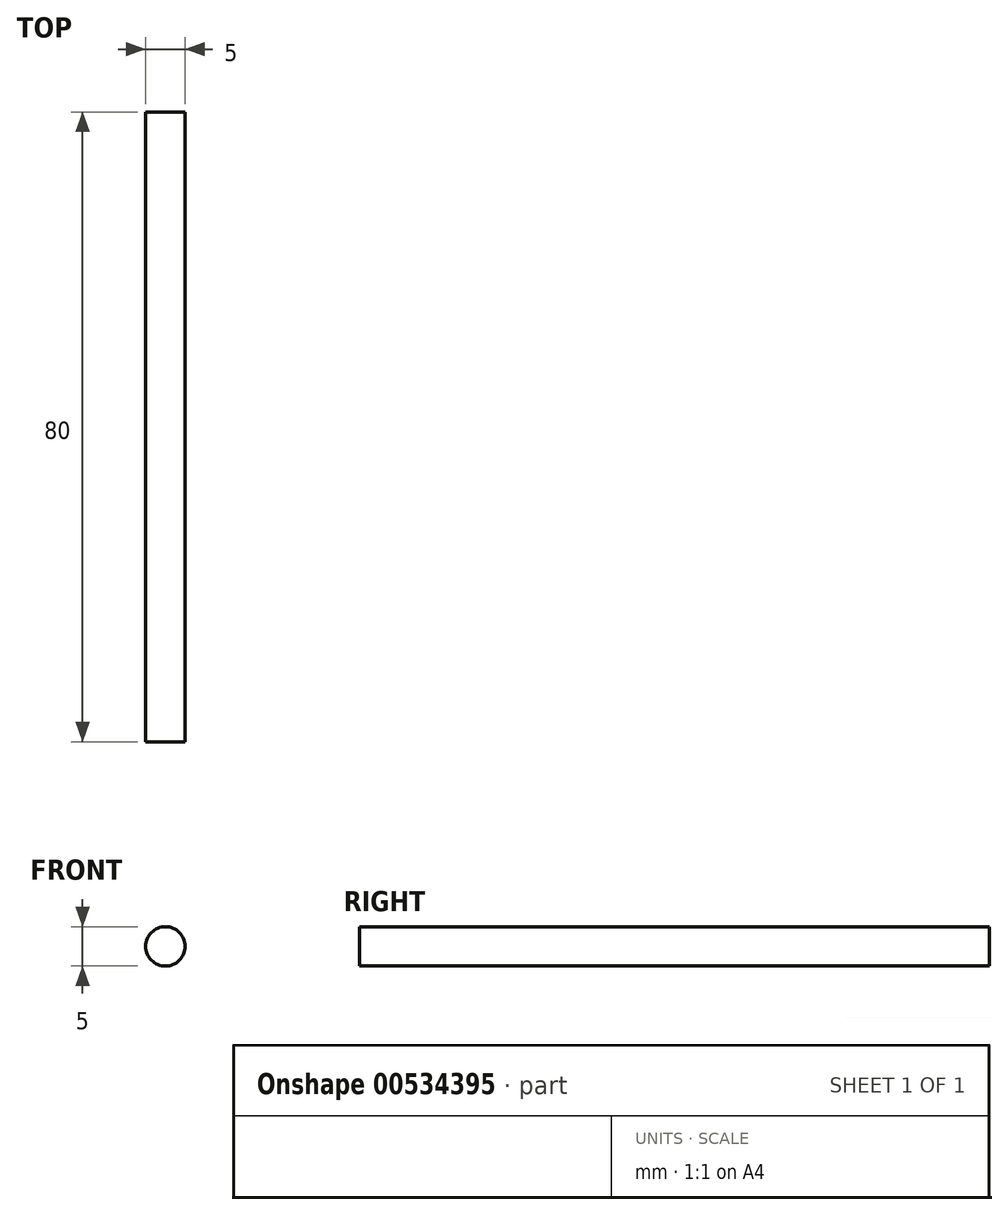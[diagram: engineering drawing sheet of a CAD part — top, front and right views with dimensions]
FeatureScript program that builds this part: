
annotation { "Feature Type Name" : "Feature", "Feature Type Description" : "" }
export const myFeature = defineFeature(function(context is Context, id is Id, definition is map)
    precondition{}
    {
        {
            var Q0;
            Q0=qCreatedBy(makeId("Front.planeOp"),FACE);
            var sketch = newSketch(context, id + "F0", { "sketchPlane" : qUnion([Q0])});
            skCircle(sketch, "E0", {"center": v(0, 0) * mm, "radius": 2.5 * mm});
            skSolve(sketch);
        }
        {
            var Q0;
            Q0 = qSketchRegion(id + "F0", true);
            extrude(context, id + "F1", {"entities" : qUnion([Q0]), "depth" : 80 * mm, "offsetDistance" : 25 * mm});
        }
    });
